# Revit family: Redia Sensors_M30_RFA
name_source: partatom
category: Pipe Accessories
units: mm (PartAtom-declared; Revit-internal decimal feet)

## family parameters
Always vertical = Yes
Cut with Voids When Loaded = No
OmniClass Number = 23.65.55.14.17
OmniClass Title = Adjusting/Controlling Valves for Liquid Services
Part Type = Normal
Round Connector Dimension = Use Diameter
Shared = Yes
Work Plane-Based = No

## types (3) — shared parameters
Body Material = Danfoss Plastic White
Connection = M30 x 1.5
Description = Radiator Sensor
H' = 98.25 mm  [stored 0.322343 ft]
IfcExportAs = IfcActuatorType
IfcExportType = Redia Sensors
Manufacturer = Danfoss
Max Temperature Setting = 28 °C
Redia Sensor = Redia_M30_RFA : Redia Sensors_M30
Sensor Media = Liquid
URL = https://store.danfoss.com

## per-type parameters (varying)
| type | Max Capillary Tube Length | Min Temperature Setting | Model | Model Type | RS | Remote Sensor | XYadd | XYlimit | YH |
| Redia Sensors_M30_Built-in_8-28 °C | 0 mm  [stored 0 ft] | 8 °C | 015G3330,015G3338,015G3339,015G5121 | Redia Sensors_M30_Built-in_8-28 °C | 0 | No | 1100 mm | 1000 mm  [stored 3.28084 ft] | 1001.75 mm |
| Redia Sensors_M30_Remote_8-28 °C_015G3332 | 2000 mm  [stored 6.56168 ft] | 8 °C | 015G3332 | Redia Sensors_M30_Remote_8-28 °C | 1 | Yes | 600 mm | 500 mm | 501.75 mm |
| Redia Sensors_M30_Built-in_16-28 °C_015G3336 | 0 mm  [stored 0 ft] | 16 °C | 015G3336 | Redia Sensors_M30_Built-in_16-28 °C | 0 | No | 1100 mm | 1000 mm  [stored 3.28084 ft] | 1001.75 mm |

note: [stored X ft] marks values corroborated as IEEE doubles in the binary element streams (Revit-internal decimal feet)

## geometry (parser evidence)
native form markers: Blend x4, Sweep x5
no freeform markers — native parametric forms only
